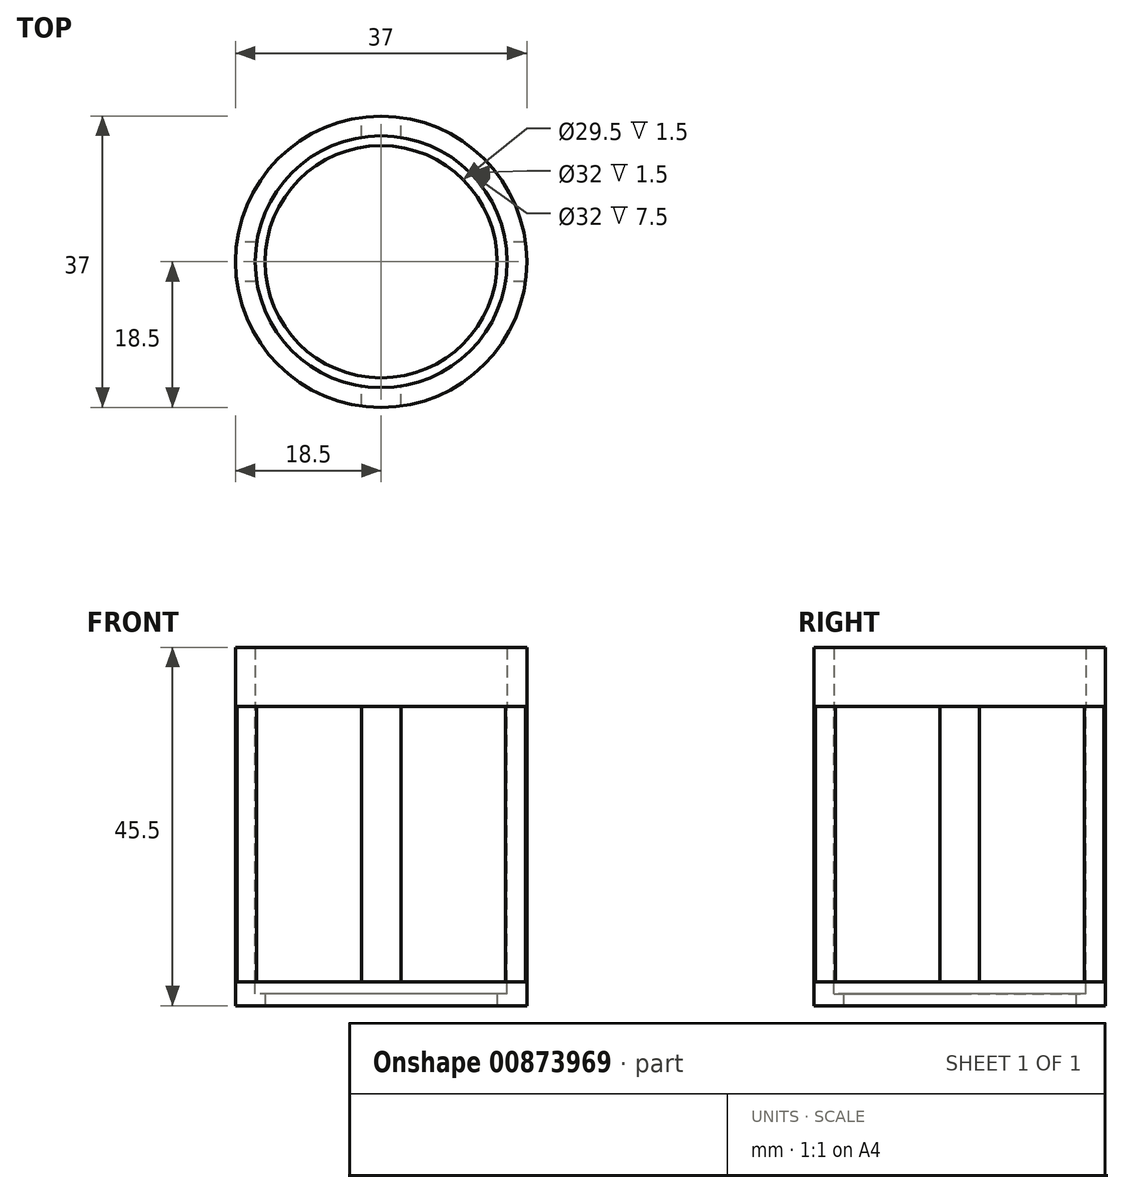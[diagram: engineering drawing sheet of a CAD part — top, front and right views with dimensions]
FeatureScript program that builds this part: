
annotation { "Feature Type Name" : "Feature", "Feature Type Description" : "" }
export const myFeature = defineFeature(function(context is Context, id is Id, definition is map)
    precondition{}
    {
        {
            var Q0;
            Q0=qCreatedBy(makeId("Top.planeOp"),FACE);
            var sketch = newSketch(context, id + "F0", { "sketchPlane" : qUnion([Q0])});
            skPoint(sketch, "E0.first.point", {"position": v(0, 0) * mm});
            skCircle(sketch, "E1", {"center": v(0, 0) * mm, "radius": 18.5 * mm});
            skCircle(sketch, "E2", {"center": v(0, 0) * mm, "radius": 14.75 * mm});
            skSolve(sketch);
        }
        {
            var Q0;
            Q0=makeQuery(id+"F0.imprint","IMPRINT",FACE,{"disambiguationData":[TD([[makeQuery(id+"F0.imprint","IMPRINT",EDGE,{"derivedFrom":sQuery(id+"F0.wireOp",EDGE,"E1")}),1.0]])]});
            extrude(context, id + "F1", {"entities" : qUnion([Q0]), "depth" : 45 * mm, "offsetDistance" : 25 * mm});
        }
        {
            var Q0;
            Q0=makeQuery(id+"F1.opExtrude","CAP_FACE",FACE,{"disambiguationData":[OSD([sQuery(id+"F0.wireOp",EDGE,"dMLi9CjI-w3AJ-lqrU-xDtC-pNT5ZKXLwRoQ"),sQuery(id+"F0.wireOp",EDGE,"p6jEfgZd-gn9l-At6D-uO4C-P7PHmhyGIQ6Y"),sQuery(id+"F0.wireOp",EDGE,"bsXDQPTp-62U9-H9b8-tNQK-BlYfqYmaa6Ta"),sQuery(id+"F0.wireOp",EDGE,"E1")])],"isStart":false});
            var sketch = newSketch(context, id + "F2", { "sketchPlane" : qUnion([Q0])});
            skCircle(sketch, "E3", {"center": v(0, 0) * mm, "radius": 14.75 * mm});
            skCircle(sketch, "E4", {"center": v(0, 0) * mm, "radius": 16 * mm});
            skSolve(sketch);
        }
        {
            var Q0;
            Q0 = qSketchRegion(id + "F2", true);
            extrude(context, id + "F3", {"entities" : qUnion([Q0]), "operationType" : NewBodyOperationType.REMOVE, "oppositeDirection" : true, "depth" : 43 * mm, "offsetDistance" : 25 * mm});
        }
        {
            var Q0;
            Q0=qCreatedBy(makeId("Top.planeOp"),FACE);
            cPlane(context, id + "F4", {"entities" : qUnion([Q0]), "cplaneType" : CPlaneType.OFFSET, "offset" : 3 * mm, "width" : 150 * mm, "height" : 150 * mm});
        }
        {
            var Q0;
            Q0=qCreatedBy(id+"F4.planeOp",FACE);
            var sketch = newSketch(context, id + "F5", { "sketchPlane" : qUnion([Q0])});
            skLineSegment(sketch, "E5.bottom", {"start": v(36.84, 2.5) * mm, "end": v(-36.84, 2.5) * mm});
            skLineSegment(sketch, "E5.top", {"start": v(36.84, -2.5) * mm, "end": v(-36.84, -2.5) * mm});
            skLineSegment(sketch, "E5.left", {"start": v(36.84, 2.5) * mm, "end": v(36.84, -2.5) * mm});
            skLineSegment(sketch, "E5.right", {"start": v(-36.84, 2.5) * mm, "end": v(-36.84, -2.5) * mm});
            skPoint(sketch, "E5.middle", {"position": v(0, 0) * mm});
            skLineSegment(sketch, "E6.bottom", {"start": v(2.5, -34.17) * mm, "end": v(-2.5, -34.17) * mm});
            skLineSegment(sketch, "E6.top", {"start": v(2.5, 34.17) * mm, "end": v(-2.5, 34.17) * mm});
            skLineSegment(sketch, "E6.left", {"start": v(2.5, -34.17) * mm, "end": v(2.5, 34.17) * mm});
            skLineSegment(sketch, "E6.right", {"start": v(-2.5, -34.17) * mm, "end": v(-2.5, 34.17) * mm});
            skSolve(sketch);
        }
        {
            var Q0;
            Q0 = qSketchRegion(id + "F5", true);
            extrude(context, id + "F6", {"entities" : qUnion([Q0]), "operationType" : NewBodyOperationType.INTERSECT, "depth" : 35 * mm, "offsetDistance" : 25 * mm});
        }
        {
            var Q0;
            Q0=qCreatedBy(makeId("Top.planeOp"),FACE);
            var sketch = newSketch(context, id + "F7", { "sketchPlane" : qUnion([Q0])});
            skCircle(sketch, "E7", {"center": v(0, 0) * mm, "radius": 18.5 * mm});
            skCircle(sketch, "E8", {"center": v(0, 0) * mm, "radius": 14.75 * mm});
            skSolve(sketch);
        }
        {
            var Q0;
            Q0 = qSketchRegion(id + "F7", true);
            extrude(context, id + "F8", {"entities" : qUnion([Q0]), "depth" : 3 * mm, "offsetDistance" : 25 * mm});
        }
        {
            var Q0;
            Q0=qCreatedBy(makeId("Top.planeOp"),FACE);
            cPlane(context, id + "F9", {"entities" : qUnion([Q0]), "cplaneType" : CPlaneType.OFFSET, "offset" : 38 * mm, "width" : 150 * mm, "height" : 150 * mm});
        }
        {
            var Q0;
            Q0=qCreatedBy(id+"F9.planeOp",FACE);
            var sketch = newSketch(context, id + "F10", { "sketchPlane" : qUnion([Q0])});
            skCircle(sketch, "E9", {"center": v(0, 0) * mm, "radius": 18.5 * mm});
            skCircle(sketch, "E10", {"center": v(0, 0) * mm, "radius": 16 * mm});
            skSolve(sketch);
        }
        {
            var Q0;
            Q0 = qSketchRegion(id + "F10", true);
            extrude(context, id + "F11", {"entities" : qUnion([Q0]), "depth" : 7.5 * mm, "offsetDistance" : 25 * mm});
        }
        {
            var Q0;
            Q0=makeQuery(id+"F8.opExtrude","CAP_FACE",FACE,{"disambiguationData":[OSD([sQuery(id+"F7.wireOp",EDGE,"E7"),sQuery(id+"F7.wireOp",EDGE,"E8")])],"isStart":false});
            var sketch = newSketch(context, id + "F12", { "sketchPlane" : qUnion([Q0])});
            skCircle(sketch, "E11", {"center": v(0, 0) * mm, "radius": 16 * mm});
            skSolve(sketch);
        }
        {
            var Q0;
            Q0 = qSketchRegion(id + "F12", true);
            extrude(context, id + "F13", {"entities" : qUnion([Q0]), "operationType" : NewBodyOperationType.REMOVE, "oppositeDirection" : true, "depth" : 1.5 * mm, "offsetDistance" : 25 * mm});
        }
    });
